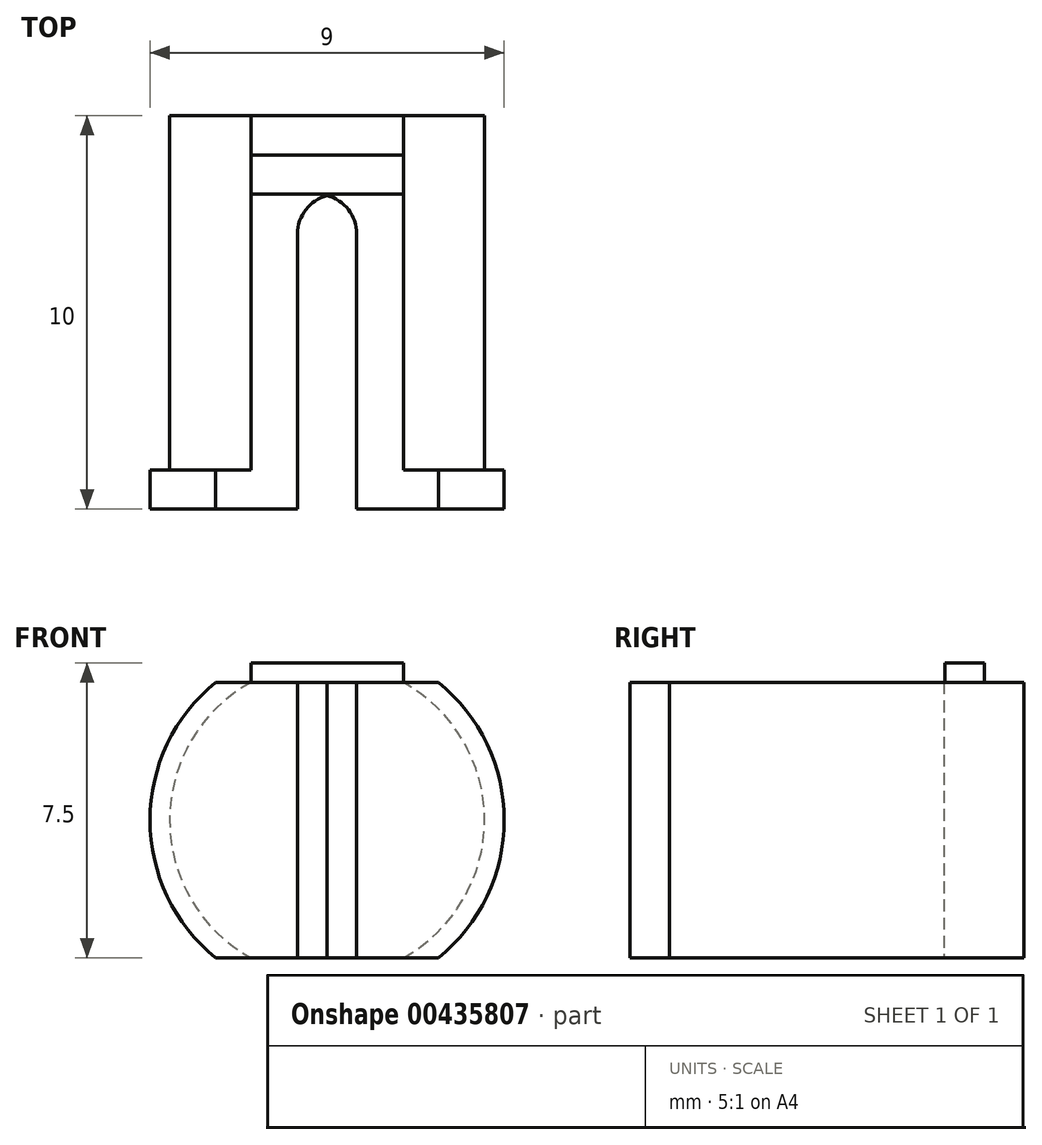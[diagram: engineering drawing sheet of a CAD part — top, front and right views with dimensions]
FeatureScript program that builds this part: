
annotation { "Feature Type Name" : "Feature", "Feature Type Description" : "" }
export const myFeature = defineFeature(function(context is Context, id is Id, definition is map)
    precondition{}
    {
        {
            var Q0;
            Q0=qCreatedBy(makeId("Front.planeOp"),FACE);
            var sketch = newSketch(context, id + "F0", { "sketchPlane" : qUnion([Q0])});
            skCircle(sketch, "E0", {"center": v(0, 0) * mm, "radius": 4 * mm});
            skLineSegment(sketch, "E1", {"start": v(-1.94, 3.5) * mm, "end": v(1.94, 3.5) * mm});
            skLineSegment(sketch, "E2", {"start": v(-1.94, -3.5) * mm, "end": v(1.94, -3.5) * mm});
            skSolve(sketch);
        }
        {
            var Q0;
            {var subQ0=sQuery(id+"F0.wireOp",EDGE,"E1");Q0=makeQuery(id+"F0.imprint","IMPRINT",FACE,{"disambiguationData":[TD([[makeQuery(id+"F0.imprint","IMPRINT",EDGE,{"derivedFrom":subQ0}),-1.0]])]});}
            extrude(context, id + "F1", {"entities" : qUnion([Q0]), "depth" : 10 * mm, "offsetDistance" : 25 * mm});
        }
        {
            var Q0;
            Q0=makeQuery(id+"F1.opExtrude","CAP_FACE",FACE,{"disambiguationData":[OSD([sQuery(id+"F0.wireOp",EDGE,"E0"),sQuery(id+"F0.wireOp",EDGE,"E1"),sQuery(id+"F0.wireOp",EDGE,"E2")])],"isStart":false});
            var sketch = newSketch(context, id + "F2", { "sketchPlane" : qUnion([Q0])});
            skCircle(sketch, "E3", {"center": v(0, 0) * mm, "radius": 4.5 * mm});
            skLineSegment(sketch, "E4", {"start": v(-2.83, 3.5) * mm, "end": v(2.83, 3.5) * mm});
            skPoint(sketch, "E4.startSnap0", {"position": v(0, 3.5) * mm});
            skLineSegment(sketch, "E5", {"start": v(-2.83, -3.5) * mm, "end": v(2.83, -3.5) * mm});
            skLineSegment(sketch, "E6", {"start": v(0.75, 3.5) * mm, "end": v(0.75, -3.5) * mm});
            skLineSegment(sketch, "E7", {"start": v(-0.75, 3.5) * mm, "end": v(-0.75, -3.5) * mm});
            skSolve(sketch);
        }
        {
            var Q0;
            {var subQ5=sQuery(id+"F0.wireOp",EDGE,"E0");var subQ6=makeQuery(id+"F1.opExtrude","CAP_EDGE",EDGE,{"disambiguationData":[OSD([subQ5]),TDD([makeQuery(id+"F0.imprint","IMPRINT",EDGE,{"disambiguationData":[TD([[makeQuery(id+"F0.imprint","INTERSECT",VERTEX,{"disambiguationData":[OD(1.0)],"derivedFrom":[subQ5,sQuery(id+"F0.wireOp",EDGE,"E1")]}),1.0]])],"derivedFrom":subQ5})])],"isStart":false});Q0=makeQuery(id+"F2.imprint","IMPRINT",FACE,{"disambiguationData":[TD([[makeQuery(id+"F2.imprint","IMPRINT",EDGE,{"derivedFrom":subQ6}),-1.0]])]});}
            var Q1;
            {var subQ5=sQuery(id+"F0.wireOp",EDGE,"E0");var subQ6=makeQuery(id+"F1.opExtrude","CAP_EDGE",EDGE,{"disambiguationData":[OSD([subQ5]),TDD([makeQuery(id+"F0.imprint","IMPRINT",EDGE,{"disambiguationData":[TD([[makeQuery(id+"F0.imprint","INTERSECT",VERTEX,{"disambiguationData":[OD(0.0)],"derivedFrom":[subQ5,sQuery(id+"F0.wireOp",EDGE,"E1")]}),-1.0]])],"derivedFrom":subQ5})])],"isStart":false});Q1=makeQuery(id+"F2.imprint","IMPRINT",FACE,{"disambiguationData":[TD([[makeQuery(id+"F2.imprint","IMPRINT",EDGE,{"derivedFrom":subQ6}),-1.0]])]});}
            extrude(context, id + "F3", {"entities" : qUnion([Q0, Q1]), "operationType" : NewBodyOperationType.ADD, "oppositeDirection" : true, "depth" : 1 * mm, "offsetDistance" : 25 * mm});
        }
        {
            var Q0;
            {var subQ0=sQuery(id+"F2.wireOp",EDGE,"E6");Q0=makeQuery(id+"F2.imprint","IMPRINT",FACE,{"disambiguationData":[TD([[makeQuery(id+"F2.imprint","IMPRINT",EDGE,{"derivedFrom":subQ0}),-1.0]])]});}
            extrude(context, id + "F4", {"entities" : qUnion([Q0]), "operationType" : NewBodyOperationType.REMOVE, "oppositeDirection" : true, "depth" : 8 * mm, "offsetDistance" : 25 * mm});
        }
        {
            var Q0;
            {var subQ0=sQuery(id+"F2.wireOp",EDGE,"E4");var subQ1=sQuery(id+"F0.wireOp",EDGE,"E1");var subQ4=sQuery(id+"F2.wireOp",EDGE,"E3");Q0=makeQuery(id+"F3.boolean.opBoolean","MERGE",FACE,{"derivedFrom":[makeQuery(id+"F1.opExtrude","SWEPT_FACE",FACE,{"disambiguationData":[OSD([subQ1])]}),makeQuery(id+"F3.opExtrude","SWEPT_FACE",FACE,{"disambiguationData":[OSD([subQ0]),TDD([makeQuery(id+"F2.imprint","IMPRINT",EDGE,{"disambiguationData":[TD([[makeQuery(id+"F2.imprint","INTERSECT",VERTEX,{"disambiguationData":[OD(0.0)],"derivedFrom":[subQ4,subQ0]}),-1.0]])],"derivedFrom":subQ0})])]}),makeQuery(id+"F3.opExtrude","SWEPT_FACE",FACE,{"disambiguationData":[OSD([subQ0]),TDD([makeQuery(id+"F2.imprint","IMPRINT",EDGE,{"disambiguationData":[TD([[makeQuery(id+"F2.imprint","INTERSECT",VERTEX,{"disambiguationData":[OD(1.0)],"derivedFrom":[subQ4,subQ0]}),1.0]])],"derivedFrom":subQ0})])]})]});}
            var sketch = newSketch(context, id + "F5", { "sketchPlane" : qUnion([Q0])});
            skLineSegment(sketch, "E8.bottom", {"start": v(-1.94, -2) * mm, "end": v(1.94, -2) * mm});
            skLineSegment(sketch, "E8.top", {"start": v(-1.94, -1) * mm, "end": v(1.94, -1) * mm});
            skLineSegment(sketch, "E8.left", {"start": v(-1.94, -2) * mm, "end": v(-1.94, -1) * mm});
            skLineSegment(sketch, "E8.right", {"start": v(1.94, -2) * mm, "end": v(1.94, -1) * mm});
            skSolve(sketch);
        }
        {
            var Q0;
            {var subQ0=sQuery(id+"F2.wireOp",EDGE,"E3");Q0=makeQuery(id+"F3.opExtrude","CAP_EDGE",EDGE,{"disambiguationData":[OSD([subQ0]),TDD([makeQuery(id+"F2.imprint","IMPRINT",EDGE,{"disambiguationData":[TD([[makeQuery(id+"F2.imprint","INTERSECT",VERTEX,{"disambiguationData":[OD(1.0)],"derivedFrom":[subQ0,sQuery(id+"F2.wireOp",EDGE,"E4")]}),1.0]])],"derivedFrom":subQ0})])],"isStart":true});}
            var Q1;
            {var subQ0=sQuery(id+"F2.wireOp",EDGE,"E3");Q1=makeQuery(id+"F3.opExtrude","CAP_EDGE",EDGE,{"disambiguationData":[OSD([subQ0]),TDD([makeQuery(id+"F2.imprint","IMPRINT",EDGE,{"disambiguationData":[TD([[makeQuery(id+"F2.imprint","INTERSECT",VERTEX,{"disambiguationData":[OD(0.0)],"derivedFrom":[subQ0,sQuery(id+"F2.wireOp",EDGE,"E4")]}),-1.0]])],"derivedFrom":subQ0})])],"isStart":true});}
            var Q2;
            Q2=makeQuery(id+"F4.boolean.opBoolean","COPY",EDGE,{"derivedFrom":makeQuery(id+"F4.opExtrude","CAP_EDGE",EDGE,{"disambiguationData":[OSD([sQuery(id+"F2.wireOp",EDGE,"E7")])],"isStart":false})});
            var Q3;
            Q3=makeQuery(id+"F4.boolean.opBoolean","COPY",EDGE,{"derivedFrom":makeQuery(id+"F4.opExtrude","CAP_EDGE",EDGE,{"disambiguationData":[OSD([sQuery(id+"F2.wireOp",EDGE,"E6")])],"isStart":false})});
            fillet(context, id + "F6", {"entities" : qUnion([Q0, Q1, Q2, Q3]), "radius" : 1 * mm, "tangentPropagation" : true, "allowEdgeOverflow" : false});
        }
        {
            var Q0;
            Q0=makeQuery(id+"F5.imprint","IMPRINT",FACE,{"disambiguationData":[TD([[makeQuery(id+"F5.imprint","IMPRINT",EDGE,{"derivedFrom":sQuery(id+"F5.wireOp",EDGE,"E8.top")}),-1.0]])]});
            extrude(context, id + "F7", {"entities" : qUnion([Q0]), "operationType" : NewBodyOperationType.ADD, "depth" : .5 * mm, "offsetDistance" : 25 * mm});
        }
    });
